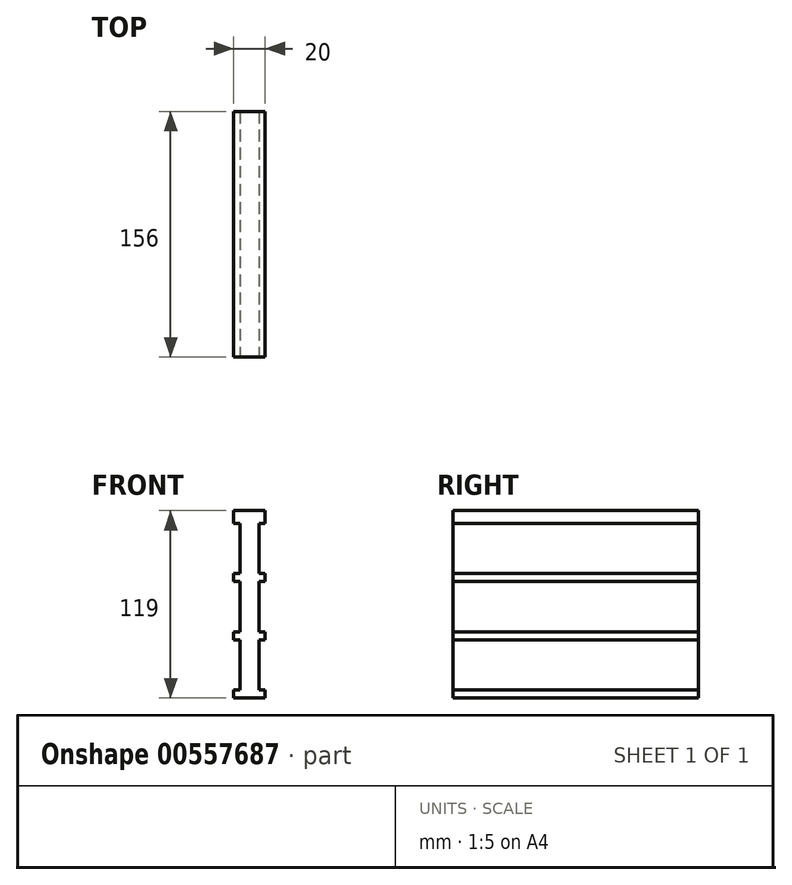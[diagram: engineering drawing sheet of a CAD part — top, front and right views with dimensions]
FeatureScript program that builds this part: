
annotation { "Feature Type Name" : "Feature", "Feature Type Description" : "" }
export const myFeature = defineFeature(function(context is Context, id is Id, definition is map)
    precondition{}
    {
        {
            assignVariable(context, id + "F0", {"name" : "box_b", "anyValue" : 166});
        }
        {
            assignVariable(context, id + "F1", {"name" : "brett_t", "anyValue" : getVariable(context, 'box_b') - 10});
        }
        {
            var Q0;
            Q0=qCreatedBy(makeId("Front.planeOp"),FACE);
            var sketch = newSketch(context, id + "F2", { "sketchPlane" : qUnion([Q0])});
            skLineSegment(sketch, "E0", {"start": v(0, 0) * mm, "end": v(0, 5) * mm});
            skLineSegment(sketch, "E1", {"start": v(0, 5) * mm, "end": v(4, 5) * mm});
            skLineSegment(sketch, "E2", {"start": v(4, 5) * mm, "end": v(4, 37) * mm});
            skLineSegment(sketch, "E3", {"start": v(4, 37) * mm, "end": v(0, 37) * mm});
            skLineSegment(sketch, "E4", {"start": v(0, 37) * mm, "end": v(0, 42) * mm});
            skLineSegment(sketch, "E5", {"start": v(0, 42) * mm, "end": v(4, 42) * mm});
            skLineSegment(sketch, "E6", {"start": v(4, 42) * mm, "end": v(4, 74) * mm});
            skLineSegment(sketch, "E7", {"start": v(4, 74) * mm, "end": v(0, 74) * mm});
            skLineSegment(sketch, "E8", {"start": v(0, 74) * mm, "end": v(0, 79) * mm});
            skLineSegment(sketch, "E9", {"start": v(0, 79) * mm, "end": v(4, 79) * mm});
            skLineSegment(sketch, "E10", {"start": v(4, 79) * mm, "end": v(4, 111) * mm});
            skLineSegment(sketch, "E11", {"start": v(4, 111) * mm, "end": v(0, 111) * mm});
            skLineSegment(sketch, "E12", {"start": v(0, 111) * mm, "end": v(0, 119) * mm});
            skLineSegment(sketch, "E13", {"start": v(0, 119) * mm, "end": v(20, 119) * mm});
            skLineSegment(sketch, "E14", {"start": v(20, 119) * mm, "end": v(20, 111) * mm});
            skLineSegment(sketch, "E15", {"start": v(20, 111) * mm, "end": v(16, 111) * mm});
            skLineSegment(sketch, "E16", {"start": v(16, 111) * mm, "end": v(16, 79) * mm});
            skLineSegment(sketch, "E17", {"start": v(16, 79) * mm, "end": v(20, 79) * mm});
            skLineSegment(sketch, "E18", {"start": v(20, 79) * mm, "end": v(20, 74) * mm});
            skLineSegment(sketch, "E19", {"start": v(20, 74) * mm, "end": v(16, 74) * mm});
            skLineSegment(sketch, "E20", {"start": v(16, 74) * mm, "end": v(16, 42) * mm});
            skLineSegment(sketch, "E21", {"start": v(16, 42) * mm, "end": v(20, 42) * mm});
            skLineSegment(sketch, "E22", {"start": v(20, 42) * mm, "end": v(20, 37) * mm});
            skLineSegment(sketch, "E23", {"start": v(20, 37) * mm, "end": v(16, 37) * mm});
            skLineSegment(sketch, "E24", {"start": v(16, 37) * mm, "end": v(16, 5) * mm});
            skLineSegment(sketch, "E25", {"start": v(16, 5) * mm, "end": v(20, 5) * mm});
            skLineSegment(sketch, "E26", {"start": v(20, 5) * mm, "end": v(20, 0) * mm});
            skLineSegment(sketch, "E27", {"start": v(20, 0) * mm, "end": v(0, 0) * mm});
            skSolve(sketch);
        }
        {
            var Q0;
            Q0=makeQuery(id+"F2.imprint","IMPRINT",FACE,{"disambiguationData":[TD([[makeQuery(id+"F2.imprint","IMPRINT",EDGE,{"derivedFrom":sQuery(id+"F2.wireOp",EDGE,"E0")}),-1.0]])]});
            extrude(context, id + "F3", {"entities" : qUnion([Q0]), "oppositeDirection" : true, "depth" : (getVariable(context, 'brett_t')) * mm, "offsetDistance" : 25 * mm});
        }
    });
